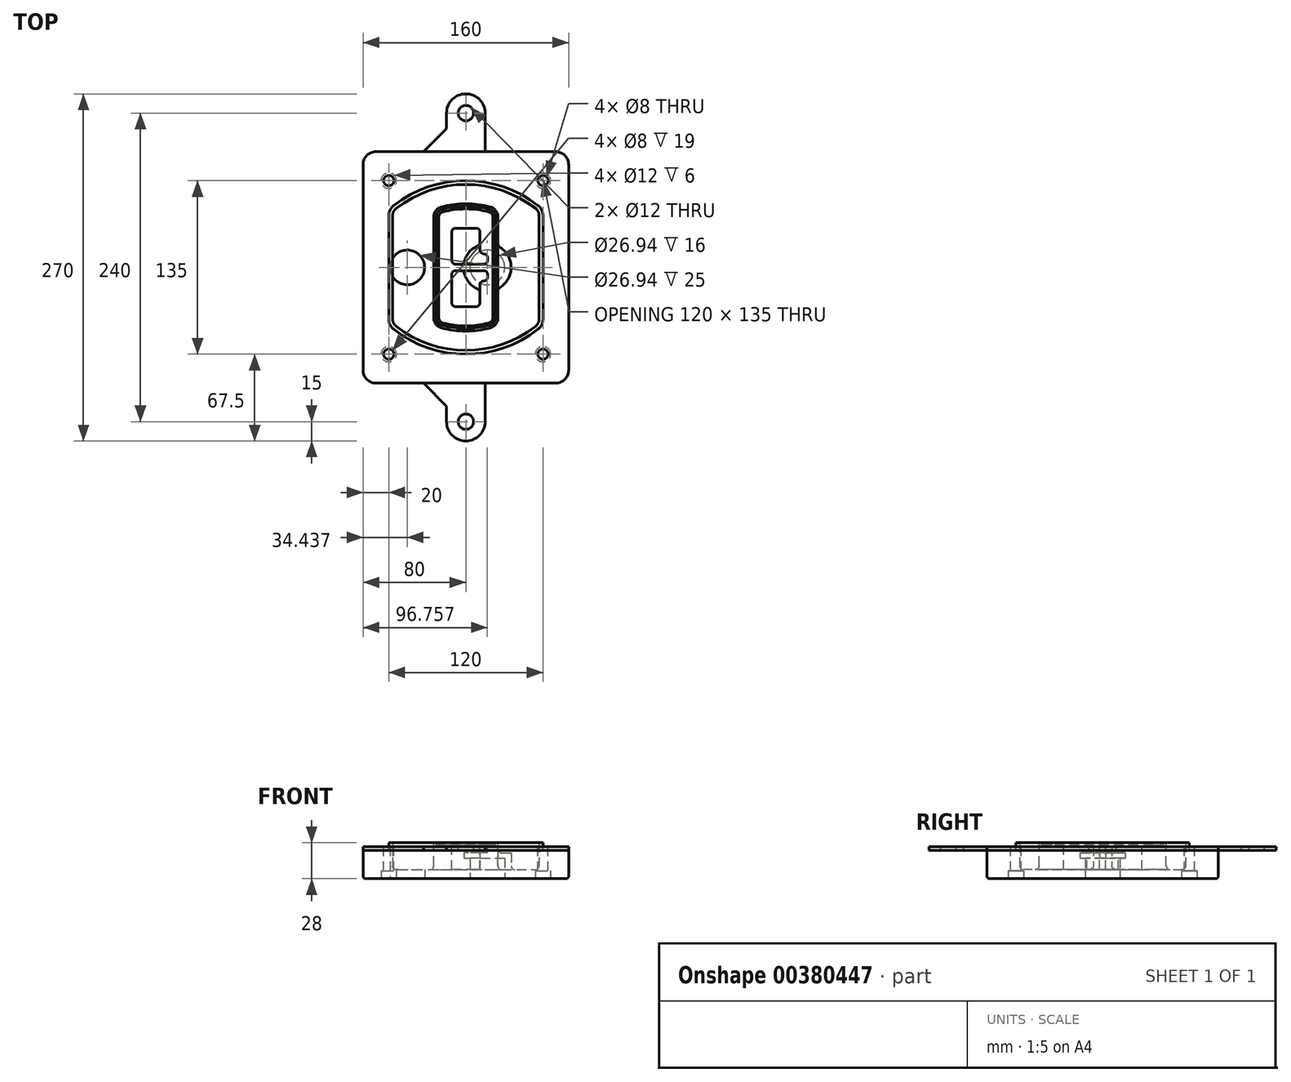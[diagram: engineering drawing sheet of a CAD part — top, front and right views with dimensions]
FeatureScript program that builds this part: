
annotation { "Feature Type Name" : "Feature", "Feature Type Description" : "" }
export const myFeature = defineFeature(function(context is Context, id is Id, definition is map)
    precondition{}
    {
        {
            var Q0;
            Q0=qCreatedBy(makeId("Top.planeOp"),FACE);
            var sketch = newSketch(context, id + "F0", { "sketchPlane" : qUnion([Q0])});
            skPoint(sketch, "E0.rect.middle", {"position": v(0, 0) * mm});
            skLineSegment(sketch, "E1.bottom", {"start": v(-70, -90) * mm, "end": v(70, -90) * mm});
            skLineSegment(sketch, "E1.top", {"start": v(-70, 90) * mm, "end": v(70, 90) * mm});
            skLineSegment(sketch, "E1.left", {"start": v(-80, -80) * mm, "end": v(-80, 80) * mm});
            skLineSegment(sketch, "E1.right", {"start": v(80, -80) * mm, "end": v(80, 80) * mm});
            skLineSegment(sketch, "E2", {"start": v(-80, 90) * mm, "end": v(80, -90) * mm, "construction": true});
            skLineSegment(sketch, "E3", {"start": v(80, 90) * mm, "end": v(-80, -90) * mm, "construction": true});
            skCircle(sketch, "E4", {"center": v(-60, 67.5) * mm, "radius": 4 * mm});
            skCircle(sketch, "E5", {"center": v(60, 67.5) * mm, "radius": 4 * mm});
            skCircle(sketch, "E6", {"center": v(60, -67.5) * mm, "radius": 4 * mm});
            skCircle(sketch, "E7", {"center": v(-60, -67.5) * mm, "radius": 4 * mm});
            skLineSegment(sketch, "E8", {"start": v(-60, 67.5) * mm, "end": v(60, 67.5) * mm, "construction": true});
            skLineSegment(sketch, "E9", {"start": v(60, 67.5) * mm, "end": v(60, -67.5) * mm, "construction": true});
            skLineSegment(sketch, "E10", {"start": v(60, -67.5) * mm, "end": v(-60, -67.5) * mm, "construction": true});
            skLineSegment(sketch, "E11", {"start": v(-60, -67.5) * mm, "end": v(-60, 67.5) * mm, "construction": true});
            skLineSegment(sketch, "E12", {"start": v(-60, 40.3) * mm, "end": v(-60, -40.3) * mm});
            skLineSegment(sketch, "E13", {"start": v(60, 40.3) * mm, "end": v(60, -40.3) * mm});
            skArc(sketch, "E14", {"start": v(56.15, 48.18) * mm, "mid": v(0, 67.5) * mm, "end": v(-56.15, 48.18) * mm});
            skArc(sketch, "E15", {"start": v(-56.15, -48.18) * mm, "mid": v(0, -67.5) * mm, "end": v(56.15, -48.18) * mm});
            skLineSegment(sketch, "E16", {"start": v(-60, 0) * mm, "end": v(60, 0) * mm, "construction": true});
            skPoint(sketch, "E17.visualSharp", {"position": v(-60, -45) * mm});
            skArc(sketch, "E17.filletArc", {"start": v(-60, -40.3) * mm, "mid": v(-58.99, -44.68) * mm, "end": v(-56.15, -48.18) * mm});
            skPoint(sketch, "E18.visualSharp", {"position": v(-60, 45) * mm});
            skArc(sketch, "E18.filletArc", {"start": v(-56.15, 48.18) * mm, "mid": v(-58.99, 44.68) * mm, "end": v(-60, 40.3) * mm});
            skPoint(sketch, "E19.visualSharp", {"position": v(60, 45) * mm});
            skArc(sketch, "E19.filletArc", {"start": v(60, 40.3) * mm, "mid": v(58.99, 44.68) * mm, "end": v(56.15, 48.18) * mm});
            skPoint(sketch, "E20.visualSharp", {"position": v(60, -45) * mm});
            skArc(sketch, "E20.filletArc", {"start": v(56.15, -48.18) * mm, "mid": v(58.99, -44.68) * mm, "end": v(60, -40.3) * mm});
            skPoint(sketch, "E21.visualSharp", {"position": v(-80, 90) * mm});
            skArc(sketch, "E21.filletArc", {"start": v(-70, 90) * mm, "mid": v(-77.07, 87.07) * mm, "end": v(-80, 80) * mm});
            skPoint(sketch, "E22.visualSharp", {"position": v(80, 90) * mm});
            skArc(sketch, "E22.filletArc", {"start": v(80, 80) * mm, "mid": v(77.07, 87.07) * mm, "end": v(70, 90) * mm});
            skPoint(sketch, "E23.visualSharp", {"position": v(80, -90) * mm});
            skArc(sketch, "E23.filletArc", {"start": v(70, -90) * mm, "mid": v(77.07, -87.07) * mm, "end": v(80, -80) * mm});
            skPoint(sketch, "E24.visualSharp", {"position": v(-80, -90) * mm});
            skArc(sketch, "E24.filletArc", {"start": v(-80, -80) * mm, "mid": v(-77.07, -87.07) * mm, "end": v(-70, -90) * mm});
            skArc(sketch, "E25.0", {"start": v(57, 40.3) * mm, "mid": v(56.3, 43.36) * mm, "end": v(54.3, 45.81) * mm});
            skLineSegment(sketch, "E25.1", {"start": v(57, 40.3) * mm, "end": v(57, -40.3) * mm});
            skArc(sketch, "E25.2", {"start": v(54.3, -45.81) * mm, "mid": v(56.3, -43.36) * mm, "end": v(57, -40.3) * mm});
            skArc(sketch, "E25.3", {"start": v(-54.3, -45.81) * mm, "mid": v(0, -64.5) * mm, "end": v(54.3, -45.81) * mm});
            skArc(sketch, "E25.4", {"start": v(-57, -40.3) * mm, "mid": v(-56.3, -43.36) * mm, "end": v(-54.3, -45.81) * mm});
            skArc(sketch, "E25.5", {"start": v(54.3, 45.81) * mm, "mid": v(0, 64.5) * mm, "end": v(-54.3, 45.81) * mm});
            skLineSegment(sketch, "E25.6", {"start": v(-57, 40.3) * mm, "end": v(-57, -40.3) * mm});
            skArc(sketch, "E25.7", {"start": v(-54.3, 45.81) * mm, "mid": v(-56.3, 43.36) * mm, "end": v(-57, 40.3) * mm});
            skArc(sketch, "E26.0", {"start": v(-58.62, 51.33) * mm, "mid": v(-62.58, 46.43) * mm, "end": v(-64, 40.3) * mm});
            skArc(sketch, "E26.1", {"start": v(58.62, 51.33) * mm, "mid": v(0, 71.5) * mm, "end": v(-58.62, 51.33) * mm});
            skArc(sketch, "E26.2", {"start": v(64, 40.3) * mm, "mid": v(62.58, 46.43) * mm, "end": v(58.62, 51.33) * mm});
            skLineSegment(sketch, "E26.3", {"start": v(64, 40.3) * mm, "end": v(64, -40.3) * mm});
            skArc(sketch, "E26.4", {"start": v(58.62, -51.33) * mm, "mid": v(62.58, -46.43) * mm, "end": v(64, -40.3) * mm});
            skLineSegment(sketch, "E26.5", {"start": v(-64, 40.3) * mm, "end": v(-64, -40.3) * mm});
            skArc(sketch, "E26.6", {"start": v(-58.62, -51.33) * mm, "mid": v(0, -71.5) * mm, "end": v(58.62, -51.33) * mm});
            skArc(sketch, "E26.7", {"start": v(-64, -40.3) * mm, "mid": v(-62.58, -46.43) * mm, "end": v(-58.62, -51.33) * mm});
            skSolve(sketch);
        }
        {
            var Q0;
            Q0=makeQuery(id+"F0.imprint","IMPRINT",FACE,{"disambiguationData":[TD([[makeQuery(id+"F0.imprint","IMPRINT",EDGE,{"derivedFrom":sQuery(id+"F0.wireOp",EDGE,"E1.bottom")}),1.0]])]});
            var Q1;
            Q1=makeQuery(id+"F0.imprint","IMPRINT",FACE,{"disambiguationData":[TD([[makeQuery(id+"F0.imprint","IMPRINT",EDGE,{"derivedFrom":sQuery(id+"F0.wireOp",EDGE,"E12")}),1.0]])]});
            var Q2;
            Q2=makeQuery(id+"F0.imprint","IMPRINT",FACE,{"disambiguationData":[TD([[makeQuery(id+"F0.imprint","IMPRINT",EDGE,{"derivedFrom":sQuery(id+"F0.wireOp",EDGE,"E25.0")}),1.0]])]});
            var Q3;
            Q3=makeQuery(id+"F0.imprint","IMPRINT",FACE,{"disambiguationData":[TD([[makeQuery(id+"F0.imprint","IMPRINT",EDGE,{"derivedFrom":sQuery(id+"F0.wireOp",EDGE,"E12")}),-1.0]])]});
            extrude(context, id + "F1", {"entities" : qUnion([Q0, Q1, Q2, Q3]), "oppositeDirection" : true, "depth" : 25 * mm});
        }
        {
            var Q0;
            Q0=makeQuery(id+"F0.imprint","IMPRINT",FACE,{"disambiguationData":[TD([[makeQuery(id+"F0.imprint","IMPRINT",EDGE,{"derivedFrom":sQuery(id+"F0.wireOp",EDGE,"E12")}),1.0]])]});
            extrude(context, id + "F2", {"entities" : qUnion([Q0]), "operationType" : NewBodyOperationType.ADD, "depth" : 3 * mm});
        }
        {
            var Q0;
            Q0=makeQuery(id+"F0.imprint","IMPRINT",FACE,{"disambiguationData":[TD([[makeQuery(id+"F0.imprint","IMPRINT",EDGE,{"derivedFrom":sQuery(id+"F0.wireOp",EDGE,"E25.0")}),1.0]])]});
            extrude(context, id + "F3", {"entities" : qUnion([Q0]), "operationType" : NewBodyOperationType.REMOVE, "oppositeDirection" : true, "depth" : 18 * mm});
        }
        {
            var Q0;
            Q0=makeQuery(id+"F2.opExtrude","CAP_FACE",FACE,{"disambiguationData":[OSD([sQuery(id+"F0.wireOp",EDGE,"E12"),sQuery(id+"F0.wireOp",EDGE,"E13"),sQuery(id+"F0.wireOp",EDGE,"E14"),sQuery(id+"F0.wireOp",EDGE,"E15"),sQuery(id+"F0.wireOp",EDGE,"E17.filletArc"),sQuery(id+"F0.wireOp",EDGE,"E18.filletArc"),sQuery(id+"F0.wireOp",EDGE,"E19.filletArc"),sQuery(id+"F0.wireOp",EDGE,"E20.filletArc"),sQuery(id+"F0.wireOp",EDGE,"E25.0"),sQuery(id+"F0.wireOp",EDGE,"E25.1"),sQuery(id+"F0.wireOp",EDGE,"E25.2"),sQuery(id+"F0.wireOp",EDGE,"E25.3"),sQuery(id+"F0.wireOp",EDGE,"E25.4"),sQuery(id+"F0.wireOp",EDGE,"E25.5"),sQuery(id+"F0.wireOp",EDGE,"E25.6"),sQuery(id+"F0.wireOp",EDGE,"E25.7")])],"isStart":false});
            var sketch = newSketch(context, id + "F4", { "sketchPlane" : qUnion([Q0])});
            skArc(sketch, "E27.0", {"start": v(-19.08, -46.97) * mm, "mid": v(0, -49.5) * mm, "end": v(19.08, -46.97) * mm});
            skArc(sketch, "E28.0", {"start": v(19.08, 46.97) * mm, "mid": v(0, 49.5) * mm, "end": v(-19.08, 46.97) * mm});
            skLineSegment(sketch, "E29", {"start": v(-25, 39.25) * mm, "end": v(-25, -39.25) * mm});
            skLineSegment(sketch, "E30", {"start": v(25, 39.25) * mm, "end": v(25, -39.25) * mm});
            skLineSegment(sketch, "E31", {"start": v(-25, 45.1) * mm, "end": v(25, 45.1) * mm, "construction": true});
            skLineSegment(sketch, "E32", {"start": v(-25, -45.1) * mm, "end": v(25, -45.1) * mm, "construction": true});
            skPoint(sketch, "E33.visualSharp", {"position": v(-25, 45.1) * mm});
            skArc(sketch, "E33.filletArc", {"start": v(-19.08, 46.97) * mm, "mid": v(-23.35, 44.11) * mm, "end": v(-25, 39.25) * mm});
            skPoint(sketch, "E34.visualSharp", {"position": v(25, 45.1) * mm});
            skArc(sketch, "E34.filletArc", {"start": v(25, 39.25) * mm, "mid": v(23.35, 44.11) * mm, "end": v(19.08, 46.97) * mm});
            skPoint(sketch, "E35.visualSharp", {"position": v(25, -45.1) * mm});
            skArc(sketch, "E35.filletArc", {"start": v(19.08, -46.97) * mm, "mid": v(23.35, -44.11) * mm, "end": v(25, -39.25) * mm});
            skPoint(sketch, "E36.visualSharp", {"position": v(-25, -45.1) * mm});
            skArc(sketch, "E36.filletArc", {"start": v(-25, -39.25) * mm, "mid": v(-23.35, -44.11) * mm, "end": v(-19.08, -46.97) * mm});
            skArc(sketch, "E37.0", {"start": v(54.3, 45.81) * mm, "mid": v(0, 64.5) * mm, "end": v(-54.3, 45.81) * mm});
            skArc(sketch, "E37.1", {"start": v(-54.3, 45.81) * mm, "mid": v(-56.3, 43.36) * mm, "end": v(-57, 40.3) * mm});
            skLineSegment(sketch, "E37.2", {"start": v(-57, 40.3) * mm, "end": v(-57, -40.3) * mm});
            skArc(sketch, "E37.3", {"start": v(-57, -40.3) * mm, "mid": v(-56.3, -43.36) * mm, "end": v(-54.3, -45.81) * mm});
            skArc(sketch, "E37.4", {"start": v(-54.3, -45.81) * mm, "mid": v(0, -64.5) * mm, "end": v(54.3, -45.81) * mm});
            skArc(sketch, "E37.5", {"start": v(54.3, -45.81) * mm, "mid": v(56.3, -43.36) * mm, "end": v(57, -40.3) * mm});
            skLineSegment(sketch, "E37.6", {"start": v(57, 40.3) * mm, "end": v(57, -40.3) * mm});
            skArc(sketch, "E37.7", {"start": v(57, 40.3) * mm, "mid": v(56.3, 43.36) * mm, "end": v(54.3, 45.81) * mm});
            skLineSegment(sketch, "E38.0", {"start": v(23, 39.25) * mm, "end": v(23, -39.25) * mm});
            skArc(sketch, "E38.1", {"start": v(18.56, -45.04) * mm, "mid": v(21.76, -42.9) * mm, "end": v(23, -39.25) * mm});
            skArc(sketch, "E38.2", {"start": v(-18.56, -45.04) * mm, "mid": v(0, -47.5) * mm, "end": v(18.56, -45.04) * mm});
            skArc(sketch, "E38.3", {"start": v(-23, -39.25) * mm, "mid": v(-21.76, -42.9) * mm, "end": v(-18.56, -45.04) * mm});
            skLineSegment(sketch, "E38.4", {"start": v(-23, 39.25) * mm, "end": v(-23, -39.25) * mm});
            skArc(sketch, "E38.5", {"start": v(23, 39.25) * mm, "mid": v(21.76, 42.9) * mm, "end": v(18.56, 45.04) * mm});
            skArc(sketch, "E38.6", {"start": v(-18.56, 45.04) * mm, "mid": v(-21.76, 42.9) * mm, "end": v(-23, 39.25) * mm});
            skArc(sketch, "E38.7", {"start": v(18.56, 45.04) * mm, "mid": v(0, 47.5) * mm, "end": v(-18.56, 45.04) * mm});
            skArc(sketch, "E39.0", {"start": v(21, 39.25) * mm, "mid": v(20.18, 41.68) * mm, "end": v(18.04, 43.1) * mm});
            skLineSegment(sketch, "E39.1", {"start": v(21, 39.25) * mm, "end": v(21, -39.25) * mm});
            skArc(sketch, "E39.2", {"start": v(18.04, -43.1) * mm, "mid": v(20.18, -41.68) * mm, "end": v(21, -39.25) * mm});
            skArc(sketch, "E39.3", {"start": v(-18.04, -43.1) * mm, "mid": v(0, -45.5) * mm, "end": v(18.04, -43.1) * mm});
            skArc(sketch, "E39.4", {"start": v(-21, -39.25) * mm, "mid": v(-20.18, -41.68) * mm, "end": v(-18.04, -43.1) * mm});
            skArc(sketch, "E39.5", {"start": v(18.04, 43.1) * mm, "mid": v(0, 45.5) * mm, "end": v(-18.04, 43.1) * mm});
            skLineSegment(sketch, "E39.6", {"start": v(-21, 39.25) * mm, "end": v(-21, -39.25) * mm});
            skArc(sketch, "E39.7", {"start": v(-18.04, 43.1) * mm, "mid": v(-20.18, 41.68) * mm, "end": v(-21, 39.25) * mm});
            skLineSegment(sketch, "E40", {"start": v(-25, 0) * mm, "end": v(25, 0) * mm, "construction": true});
            skLineSegment(sketch, "E41", {"start": v(-11, 5.5) * mm, "end": v(-11, 27.5) * mm});
            skLineSegment(sketch, "E42", {"start": v(-8, 30.5) * mm, "end": v(8, 30.5) * mm});
            skLineSegment(sketch, "E43", {"start": v(11, 27.5) * mm, "end": v(11, 13.5) * mm});
            skLineSegment(sketch, "E44", {"start": v(14, 10.5) * mm, "end": v(14, 10.5) * mm});
            skLineSegment(sketch, "E45", {"start": v(17, 7.5) * mm, "end": v(17, 5.5) * mm});
            skLineSegment(sketch, "E46", {"start": v(14, 2.5) * mm, "end": v(-8, 2.5) * mm});
            skPoint(sketch, "E47.visualSharp", {"position": v(-11, 30.5) * mm});
            skArc(sketch, "E47.filletArc", {"start": v(-8, 30.5) * mm, "mid": v(-10.12, 29.62) * mm, "end": v(-11, 27.5) * mm});
            skPoint(sketch, "E48.visualSharp", {"position": v(11, 30.5) * mm});
            skArc(sketch, "E48.filletArc", {"start": v(11, 27.5) * mm, "mid": v(10.12, 29.62) * mm, "end": v(8, 30.5) * mm});
            skPoint(sketch, "E49.visualSharp", {"position": v(11, 10.5) * mm});
            skArc(sketch, "E49.filletArc", {"start": v(11, 13.5) * mm, "mid": v(11.88, 11.38) * mm, "end": v(14, 10.5) * mm});
            skPoint(sketch, "E50.visualSharp", {"position": v(17, 10.5) * mm});
            skArc(sketch, "E50.filletArc", {"start": v(17, 7.5) * mm, "mid": v(16.12, 9.62) * mm, "end": v(14, 10.5) * mm});
            skPoint(sketch, "E51.visualSharp", {"position": v(17, 2.5) * mm});
            skArc(sketch, "E51.filletArc", {"start": v(14, 2.5) * mm, "mid": v(16.12, 3.38) * mm, "end": v(17, 5.5) * mm});
            skPoint(sketch, "E52.visualSharp", {"position": v(-11, 2.5) * mm});
            skArc(sketch, "E52.filletArc", {"start": v(-11, 5.5) * mm, "mid": v(-10.12, 3.38) * mm, "end": v(-8, 2.5) * mm});
            skLineSegment(sketch, "E53.0.MirrorCS", {"start": v(14, -2.5) * mm, "end": v(-8, -2.5) * mm});
            skArc(sketch, "E54.0.MirrorCS", {"start": v(-11, -5.5) * mm, "mid": v(-10.12, -3.38) * mm, "end": v(-8, -2.5) * mm});
            skLineSegment(sketch, "E55.0.MirrorCS", {"start": v(-11, -5.5) * mm, "end": v(-11, -27.5) * mm});
            skArc(sketch, "E56.0.MirrorCS", {"start": v(-8, -30.5) * mm, "mid": v(-10.12, -29.62) * mm, "end": v(-11, -27.5) * mm});
            skLineSegment(sketch, "E57.0.MirrorCS", {"start": v(-8, -30.5) * mm, "end": v(8, -30.5) * mm});
            skArc(sketch, "E58.0.MirrorCS", {"start": v(11, -27.5) * mm, "mid": v(10.12, -29.62) * mm, "end": v(8, -30.5) * mm});
            skLineSegment(sketch, "E59.0.MirrorCS", {"start": v(11, -27.5) * mm, "end": v(11, -13.5) * mm});
            skArc(sketch, "E60.0.MirrorCS", {"start": v(11, -13.5) * mm, "mid": v(11.88, -11.38) * mm, "end": v(14, -10.5) * mm});
            skArc(sketch, "E61.0.MirrorCS", {"start": v(17, -7.5) * mm, "mid": v(16.12, -9.62) * mm, "end": v(14, -10.5) * mm});
            skLineSegment(sketch, "E62.0.MirrorCS", {"start": v(17, -7.5) * mm, "end": v(17, -5.5) * mm});
            skArc(sketch, "E63.0.MirrorCS", {"start": v(14, -2.5) * mm, "mid": v(16.12, -3.38) * mm, "end": v(17, -5.5) * mm});
            skSolve(sketch);
        }
        {
            var Q0;
            Q0=makeQuery(id+"F4.imprint","IMPRINT",FACE,{"disambiguationData":[TD([[makeQuery(id+"F4.imprint","IMPRINT",EDGE,{"derivedFrom":sQuery(id+"F4.wireOp",EDGE,"E27.0")}),1.0]])]});
            var Q1;
            Q1=makeQuery(id+"F4.imprint","IMPRINT",FACE,{"disambiguationData":[TD([[makeQuery(id+"F4.imprint","IMPRINT",EDGE,{"derivedFrom":sQuery(id+"F4.wireOp",EDGE,"E38.0")}),-1.0]])]});
            var Q2;
            Q2=makeQuery(id+"F4.imprint","IMPRINT",FACE,{"disambiguationData":[TD([[makeQuery(id+"F4.imprint","IMPRINT",EDGE,{"derivedFrom":sQuery(id+"F4.wireOp",EDGE,"E39.0")}),1.0]])]});
            extrude(context, id + "F5", {"entities" : qUnion([Q0, Q1, Q2]), "operationType" : NewBodyOperationType.ADD, "endBound" : BoundingType.UP_TO_NEXT, "oppositeDirection" : true, "depth" : 25 * mm});
        }
        {
            var Q0;
            Q0=makeQuery(id+"F4.imprint","IMPRINT",FACE,{"disambiguationData":[TD([[makeQuery(id+"F4.imprint","IMPRINT",EDGE,{"derivedFrom":sQuery(id+"F4.wireOp",EDGE,"E38.0")}),-1.0]])]});
            extrude(context, id + "F6", {"entities" : qUnion([Q0]), "operationType" : NewBodyOperationType.REMOVE, "oppositeDirection" : true, "depth" : 2 * mm});
        }
        {
            var Q0;
            Q0=makeQuery(id+"F1.opExtrude","CAP_FACE",FACE,{"disambiguationData":[OSD([sQuery(id+"F0.wireOp",EDGE,"E1.bottom"),sQuery(id+"F0.wireOp",EDGE,"E1.top"),sQuery(id+"F0.wireOp",EDGE,"E1.left"),sQuery(id+"F0.wireOp",EDGE,"E1.right"),sQuery(id+"F0.wireOp",EDGE,"E4"),sQuery(id+"F0.wireOp",EDGE,"E5"),sQuery(id+"F0.wireOp",EDGE,"E6"),sQuery(id+"F0.wireOp",EDGE,"E7"),sQuery(id+"F0.wireOp",EDGE,"E21.filletArc"),sQuery(id+"F0.wireOp",EDGE,"E22.filletArc"),sQuery(id+"F0.wireOp",EDGE,"E23.filletArc"),sQuery(id+"F0.wireOp",EDGE,"E24.filletArc")])],"isStart":false});
            var sketch = newSketch(context, id + "F7", { "sketchPlane" : qUnion([Q0])});
            skCircle(sketch, "E64", {"center": v(16.76, 0) * mm, "radius": 13.47 * mm});
            skCircle(sketch, "E65", {"center": v(-45.56, 0) * mm, "radius": 13.47 * mm});
            skLineSegment(sketch, "E66", {"start": v(80, 0) * mm, "end": v(-80, 0) * mm});
            skCircle(sketch, "E67", {"center": v(16.76, 0) * mm, "radius": 18.47 * mm});
            skCircle(sketch, "E68", {"center": v(60, -67.5) * mm, "radius": 6 * mm});
            skCircle(sketch, "E69", {"center": v(-60, -67.5) * mm, "radius": 6 * mm});
            skCircle(sketch, "E70", {"center": v(-60, 67.5) * mm, "radius": 6 * mm});
            skCircle(sketch, "E71", {"center": v(60, 67.5) * mm, "radius": 6 * mm});
            skSolve(sketch);
        }
        {
            var Q0;
            {var subQ1=sQuery(id+"F7.wireOp",EDGE,"E66");var subQ4=sQuery(id+"F7.wireOp",EDGE,"E64");var subQ6=makeQuery(id+"F7.imprint","INTERSECT",VERTEX,{"disambiguationData":[OD(0.0)],"derivedFrom":[subQ4,subQ1]});Q0=makeQuery(id+"F7.imprint","IMPRINT",FACE,{"disambiguationData":[TD([[makeQuery(id+"F7.imprint","IMPRINT",EDGE,{"disambiguationData":[TD([[subQ6,-1.0]])],"derivedFrom":subQ4}),-1.0]])]});}
            var Q1;
            {var subQ0=sQuery(id+"F7.wireOp",EDGE,"E66");var subQ1=sQuery(id+"F7.wireOp",EDGE,"E64");var subQ3=makeQuery(id+"F7.imprint","INTERSECT",VERTEX,{"disambiguationData":[OD(0.0)],"derivedFrom":[subQ1,subQ0]});Q1=makeQuery(id+"F7.imprint","IMPRINT",FACE,{"disambiguationData":[TD([[makeQuery(id+"F7.imprint","IMPRINT",EDGE,{"disambiguationData":[TD([[subQ3,-1.0]])],"derivedFrom":subQ1}),1.0]])]});}
            var Q2;
            {var subQ0=sQuery(id+"F7.wireOp",EDGE,"E66");var subQ1=sQuery(id+"F7.wireOp",EDGE,"E64");var subQ3=makeQuery(id+"F7.imprint","INTERSECT",VERTEX,{"disambiguationData":[OD(0.0)],"derivedFrom":[subQ1,subQ0]});Q2=makeQuery(id+"F7.imprint","IMPRINT",FACE,{"disambiguationData":[TD([[makeQuery(id+"F7.imprint","IMPRINT",EDGE,{"disambiguationData":[TD([[subQ3,1.0]])],"derivedFrom":subQ1}),1.0]])]});}
            var Q3;
            {var subQ1=sQuery(id+"F7.wireOp",EDGE,"E66");var subQ4=sQuery(id+"F7.wireOp",EDGE,"E64");var subQ6=makeQuery(id+"F7.imprint","INTERSECT",VERTEX,{"disambiguationData":[OD(0.0)],"derivedFrom":[subQ4,subQ1]});Q3=makeQuery(id+"F7.imprint","IMPRINT",FACE,{"disambiguationData":[TD([[makeQuery(id+"F7.imprint","IMPRINT",EDGE,{"disambiguationData":[TD([[subQ6,1.0]])],"derivedFrom":subQ4}),-1.0]])]});}
            extrude(context, id + "F8", {"entities" : qUnion([Q0, Q1, Q2, Q3]), "operationType" : NewBodyOperationType.ADD, "oppositeDirection" : true, "depth" : 20 * mm});
        }
        {
            var Q0;
            {var subQ0=sQuery(id+"F7.wireOp",EDGE,"E66");var subQ1=sQuery(id+"F7.wireOp",EDGE,"E64");var subQ3=makeQuery(id+"F7.imprint","INTERSECT",VERTEX,{"disambiguationData":[OD(0.0)],"derivedFrom":[subQ1,subQ0]});Q0=makeQuery(id+"F7.imprint","IMPRINT",FACE,{"disambiguationData":[TD([[makeQuery(id+"F7.imprint","IMPRINT",EDGE,{"disambiguationData":[TD([[subQ3,-1.0]])],"derivedFrom":subQ1}),1.0]])]});}
            var Q1;
            {var subQ0=sQuery(id+"F7.wireOp",EDGE,"E66");var subQ1=sQuery(id+"F7.wireOp",EDGE,"E64");var subQ3=makeQuery(id+"F7.imprint","INTERSECT",VERTEX,{"disambiguationData":[OD(0.0)],"derivedFrom":[subQ1,subQ0]});Q1=makeQuery(id+"F7.imprint","IMPRINT",FACE,{"disambiguationData":[TD([[makeQuery(id+"F7.imprint","IMPRINT",EDGE,{"disambiguationData":[TD([[subQ3,1.0]])],"derivedFrom":subQ1}),1.0]])]});}
            extrude(context, id + "F9", {"entities" : qUnion([Q0, Q1]), "operationType" : NewBodyOperationType.REMOVE, "oppositeDirection" : true, "depth" : 16 * mm});
        }
        {
            var Q0;
            {var subQ0=sQuery(id+"F7.wireOp",EDGE,"E66");var subQ1=sQuery(id+"F7.wireOp",EDGE,"E65");var subQ3=makeQuery(id+"F7.imprint","INTERSECT",VERTEX,{"disambiguationData":[OD(0.0)],"derivedFrom":[subQ1,subQ0]});Q0=makeQuery(id+"F7.imprint","IMPRINT",FACE,{"disambiguationData":[TD([[makeQuery(id+"F7.imprint","IMPRINT",EDGE,{"disambiguationData":[TD([[subQ3,-1.0]])],"derivedFrom":subQ1}),1.0]])]});}
            var Q1;
            {var subQ0=sQuery(id+"F7.wireOp",EDGE,"E66");var subQ1=sQuery(id+"F7.wireOp",EDGE,"E65");var subQ3=makeQuery(id+"F7.imprint","INTERSECT",VERTEX,{"disambiguationData":[OD(0.0)],"derivedFrom":[subQ1,subQ0]});Q1=makeQuery(id+"F7.imprint","IMPRINT",FACE,{"disambiguationData":[TD([[makeQuery(id+"F7.imprint","IMPRINT",EDGE,{"disambiguationData":[TD([[subQ3,1.0]])],"derivedFrom":subQ1}),1.0]])]});}
            extrude(context, id + "F10", {"entities" : qUnion([Q0, Q1]), "operationType" : NewBodyOperationType.REMOVE, "oppositeDirection" : true, "depth" : 25 * mm});
        }
        {
            var Q0;
            Q0=makeQuery(id+"F7.imprint","IMPRINT",FACE,{"disambiguationData":[TD([[makeQuery(id+"F7.imprint","IMPRINT",EDGE,{"derivedFrom":sQuery(id+"F7.wireOp",EDGE,"E68")}),1.0]])]});
            var Q1;
            Q1=makeQuery(id+"F7.imprint","IMPRINT",FACE,{"disambiguationData":[TD([[makeQuery(id+"F7.imprint","IMPRINT",EDGE,{"derivedFrom":makeQuery(id+"F1.opExtrude","CAP_EDGE",EDGE,{"disambiguationData":[OSD([sQuery(id+"F0.wireOp",EDGE,"E5")])],"isStart":false})}),-1.0]])]});
            var Q2;
            Q2=makeQuery(id+"F7.imprint","IMPRINT",FACE,{"disambiguationData":[TD([[makeQuery(id+"F7.imprint","IMPRINT",EDGE,{"derivedFrom":sQuery(id+"F7.wireOp",EDGE,"E69")}),1.0]])]});
            var Q3;
            Q3=makeQuery(id+"F7.imprint","IMPRINT",FACE,{"disambiguationData":[TD([[makeQuery(id+"F7.imprint","IMPRINT",EDGE,{"derivedFrom":makeQuery(id+"F1.opExtrude","CAP_EDGE",EDGE,{"disambiguationData":[OSD([sQuery(id+"F0.wireOp",EDGE,"E4")])],"isStart":false})}),-1.0]])]});
            var Q4;
            Q4=makeQuery(id+"F7.imprint","IMPRINT",FACE,{"disambiguationData":[TD([[makeQuery(id+"F7.imprint","IMPRINT",EDGE,{"derivedFrom":sQuery(id+"F7.wireOp",EDGE,"E70")}),1.0]])]});
            var Q5;
            Q5=makeQuery(id+"F7.imprint","IMPRINT",FACE,{"disambiguationData":[TD([[makeQuery(id+"F7.imprint","IMPRINT",EDGE,{"derivedFrom":makeQuery(id+"F1.opExtrude","CAP_EDGE",EDGE,{"disambiguationData":[OSD([sQuery(id+"F0.wireOp",EDGE,"E7")])],"isStart":false})}),-1.0]])]});
            var Q6;
            Q6=makeQuery(id+"F7.imprint","IMPRINT",FACE,{"disambiguationData":[TD([[makeQuery(id+"F7.imprint","IMPRINT",EDGE,{"derivedFrom":sQuery(id+"F7.wireOp",EDGE,"E71")}),1.0]])]});
            var Q7;
            Q7=makeQuery(id+"F7.imprint","IMPRINT",FACE,{"disambiguationData":[TD([[makeQuery(id+"F7.imprint","IMPRINT",EDGE,{"derivedFrom":makeQuery(id+"F1.opExtrude","CAP_EDGE",EDGE,{"disambiguationData":[OSD([sQuery(id+"F0.wireOp",EDGE,"E6")])],"isStart":false})}),-1.0]])]});
            extrude(context, id + "F11", {"entities" : qUnion([Q0, Q1, Q2, Q3, Q4, Q5, Q6, Q7]), "operationType" : NewBodyOperationType.REMOVE, "oppositeDirection" : true, "depth" : 6 * mm});
        }
        {
            var Q0;
            Q0=makeQuery(id+"F9.boolean.opBoolean","COPY",FACE,{"derivedFrom":makeQuery(id+"F9.opExtrude","CAP_FACE",FACE,{"disambiguationData":[OSD([sQuery(id+"F7.wireOp",EDGE,"E64")])],"isStart":false})});
            var sketch = newSketch(context, id + "F12", { "sketchPlane" : qUnion([Q0])});
            skArc(sketch, "E72.0", {"start": v(11, 17.55) * mm, "mid": v(2.57, 11.82) * mm, "end": v(-1.54, 2.5) * mm});
            skArc(sketch, "E72.1", {"start": v(-1.54, -2.5) * mm, "mid": v(2.57, -11.82) * mm, "end": v(11, -17.55) * mm});
            skLineSegment(sketch, "E73", {"start": v(-1.54, -2.5) * mm, "end": v(14, -2.5) * mm});
            skLineSegment(sketch, "E74.0", {"start": v(14, 2.5) * mm, "end": v(-1.54, 2.5) * mm});
            skArc(sketch, "E74.1", {"start": v(14, 2.5) * mm, "mid": v(16.12, 3.38) * mm, "end": v(17, 5.5) * mm});
            skLineSegment(sketch, "E74.2", {"start": v(17, 7.5) * mm, "end": v(17, 5.5) * mm});
            skArc(sketch, "E74.3", {"start": v(17, 7.5) * mm, "mid": v(16.12, 9.62) * mm, "end": v(14, 10.5) * mm});
            skArc(sketch, "E74.4", {"start": v(11, 13.5) * mm, "mid": v(11.88, 11.38) * mm, "end": v(14, 10.5) * mm});
            skLineSegment(sketch, "E74.5", {"start": v(11, 17.55) * mm, "end": v(11, 13.5) * mm});
            skLineSegment(sketch, "E74.7", {"start": v(14, -2.5) * mm, "end": v(-1.54, -2.5) * mm});
            skArc(sketch, "E74.8", {"start": v(14, -2.5) * mm, "mid": v(16.12, -3.38) * mm, "end": v(17, -5.5) * mm});
            skLineSegment(sketch, "E74.9", {"start": v(17, -7.5) * mm, "end": v(17, -5.5) * mm});
            skArc(sketch, "E74.10", {"start": v(17, -7.5) * mm, "mid": v(16.12, -9.62) * mm, "end": v(14, -10.5) * mm});
            skArc(sketch, "E74.11", {"start": v(11, -13.5) * mm, "mid": v(11.88, -11.38) * mm, "end": v(14, -10.5) * mm});
            skLineSegment(sketch, "E74.12", {"start": v(11, -17.55) * mm, "end": v(11, -13.5) * mm});
            skPoint(sketch, "E75.orphan", {"position": v(11, -27.5) * mm});
            skPoint(sketch, "E76.orphan", {"position": v(-8, -2.5) * mm});
            skPoint(sketch, "E77.orphan", {"position": v(-8, 2.5) * mm});
            skPoint(sketch, "E78.orphan", {"position": v(11, 27.5) * mm});
            skSolve(sketch);
        }
        {
            var Q0;
            {var subQ7=sQuery(id+"F12.wireOp",EDGE,"E72.0");var subQ14=sQuery(id+"F12.wireOp",EDGE,"E72.1");var subQ16=sQuery(id+"F12.wireOp",EDGE,"E74.1");var subQ18=sQuery(id+"F12.wireOp",EDGE,"E74.8");Q0=qUnion([makeQuery(id+"F12.imprint","IMPRINT",FACE,{"disambiguationData":[TD([[makeQuery(id+"F12.imprint","IMPRINT",EDGE,{"derivedFrom":subQ7}),1.0]])]}),makeQuery(id+"F12.imprint","IMPRINT",FACE,{"disambiguationData":[TD([[makeQuery(id+"F12.imprint","IMPRINT",EDGE,{"derivedFrom":subQ14}),1.0]])]}),makeQuery(id+"F12.imprint","IMPRINT",FACE,{"disambiguationData":[TD([[makeQuery(id+"F12.imprint","IMPRINT",EDGE,{"derivedFrom":subQ16}),1.0]])]}),makeQuery(id+"F12.imprint","IMPRINT",FACE,{"disambiguationData":[TD([[makeQuery(id+"F12.imprint","IMPRINT",EDGE,{"derivedFrom":subQ18}),-1.0]])]})]);}
            var Q1;
            Q1=makeQuery(id+"F5.boolean.opBoolean","SPLIT",FACE,{"disambiguationData":[TD([makeQuery(id+"F5.opExtrude","SWEPT_FACE",FACE,{"disambiguationData":[OSD([sQuery(id+"F4.wireOp",EDGE,"E41")])]})])],"derivedFrom":makeQuery(id+"F3.boolean.opBoolean","COPY",FACE,{"derivedFrom":makeQuery(id+"F3.opExtrude","CAP_FACE",FACE,{"disambiguationData":[OSD([sQuery(id+"F0.wireOp",EDGE,"E25.0"),sQuery(id+"F0.wireOp",EDGE,"E25.1"),sQuery(id+"F0.wireOp",EDGE,"E25.2"),sQuery(id+"F0.wireOp",EDGE,"E25.3"),sQuery(id+"F0.wireOp",EDGE,"E25.4"),sQuery(id+"F0.wireOp",EDGE,"E25.5"),sQuery(id+"F0.wireOp",EDGE,"E25.6"),sQuery(id+"F0.wireOp",EDGE,"E25.7")])],"isStart":false})})});
            extrude(context, id + "F13", {"entities" : qUnion([Q0]), "operationType" : NewBodyOperationType.REMOVE, "endBound" : BoundingType.UP_TO_SURFACE, "endBoundEntityFace" : qUnion([Q1]), "depth" : 25 * mm});
        }
        {
            var Q0;
            Q0=makeQuery(id+"F3.boolean.opBoolean","COPY",EDGE,{"derivedFrom":makeQuery(id+"F3.opExtrude","CAP_EDGE",EDGE,{"disambiguationData":[OSD([sQuery(id+"F0.wireOp",EDGE,"E25.6")])],"isStart":false})});
            var Q1;
            Q1=makeQuery(id+"F8.boolean.opBoolean","INTERSECT",EDGE,{"derivedFrom":[makeQuery(id+"F5.opExtrude","SWEPT_FACE",FACE,{"disambiguationData":[OSD([sQuery(id+"F4.wireOp",EDGE,"E30")])]}),makeQuery(id+"F8.opExtrude","CAP_FACE",FACE,{"disambiguationData":[OSD([sQuery(id+"F7.wireOp",EDGE,"E67")])],"isStart":false})]});
            var Q2;
            Q2=makeQuery(id+"F8.boolean.opBoolean","INTERSECT",EDGE,{"disambiguationData":[OD(1.0)],"derivedFrom":[makeQuery(id+"F5.opExtrude","SWEPT_FACE",FACE,{"disambiguationData":[OSD([sQuery(id+"F4.wireOp",EDGE,"E30")])]}),makeQuery(id+"F8.opExtrude","SWEPT_FACE",FACE,{"disambiguationData":[OSD([sQuery(id+"F7.wireOp",EDGE,"E67")])]})]});
            var Q3;
            {var subQ0=sQuery(id+"F4.wireOp",EDGE,"E30");Q3=makeQuery(id+"F8.boolean.opBoolean","SPLIT",EDGE,{"disambiguationData":[TD([makeQuery(id+"F5.opExtrude","SWEPT_FACE",FACE,{"disambiguationData":[OSD([sQuery(id+"F4.wireOp",EDGE,"E35.filletArc")])]})])],"derivedFrom":makeQuery(id+"F5.opExtrude","CAP_EDGE",EDGE,{"disambiguationData":[OSD([subQ0])],"isStart":false})});}
            var Q4;
            {var subQ0=sQuery(id+"F0.wireOp",EDGE,"E25.7");var subQ1=sQuery(id+"F0.wireOp",EDGE,"E25.1");var subQ2=sQuery(id+"F0.wireOp",EDGE,"E25.6");var subQ3=sQuery(id+"F0.wireOp",EDGE,"E25.5");var subQ4=sQuery(id+"F0.wireOp",EDGE,"E25.4");var subQ5=sQuery(id+"F0.wireOp",EDGE,"E25.0");var subQ6=sQuery(id+"F0.wireOp",EDGE,"E25.2");var subQ7=sQuery(id+"F0.wireOp",EDGE,"E25.3");Q4=makeQuery(id+"F8.boolean.opBoolean","INTERSECT",EDGE,{"derivedFrom":[makeQuery(id+"F5.boolean.opBoolean","SPLIT",FACE,{"disambiguationData":[TD([makeQuery(id+"F2.opExtrude","SWEPT_FACE",FACE,{"disambiguationData":[OSD([subQ5])]})])],"derivedFrom":makeQuery(id+"F3.boolean.opBoolean","COPY",FACE,{"derivedFrom":makeQuery(id+"F3.opExtrude","CAP_FACE",FACE,{"disambiguationData":[OSD([subQ5,subQ1,subQ6,subQ7,subQ4,subQ3,subQ2,subQ0])],"isStart":false})})}),makeQuery(id+"F8.opExtrude","SWEPT_FACE",FACE,{"disambiguationData":[OSD([sQuery(id+"F7.wireOp",EDGE,"E67")])]})]});}
            var Q5;
            Q5=makeQuery(id+"F8.boolean.opBoolean","INTERSECT",EDGE,{"disambiguationData":[OD(0.0)],"derivedFrom":[makeQuery(id+"F5.opExtrude","SWEPT_FACE",FACE,{"disambiguationData":[OSD([sQuery(id+"F4.wireOp",EDGE,"E30")])]}),makeQuery(id+"F8.opExtrude","SWEPT_FACE",FACE,{"disambiguationData":[OSD([sQuery(id+"F7.wireOp",EDGE,"E67")])]})]});
            fillet(context, id + "F14", {"entities" : qUnion([Q0, Q1, Q2, Q3, Q4, Q5]), "radius" : 3 * mm, "tangentPropagation" : true, "allowEdgeOverflow" : false});
        }
        {
            var Q0;
            Q0=makeQuery(id+"F1.opExtrude","CAP_EDGE",EDGE,{"disambiguationData":[OSD([sQuery(id+"F0.wireOp",EDGE,"E1.bottom")])],"isStart":false});
            fillet(context, id + "F15", {"entities" : qUnion([Q0]), "radius" : 2 * mm, "tangentPropagation" : true, "allowEdgeOverflow" : false});
        }
        {
            var Q0;
            {var subQ0=sQuery(id+"F0.wireOp",EDGE,"E21.filletArc");var subQ1=sQuery(id+"F0.wireOp",EDGE,"E7");var subQ2=sQuery(id+"F0.wireOp",EDGE,"E6");var subQ3=sQuery(id+"F0.wireOp",EDGE,"E5");var subQ4=sQuery(id+"F0.wireOp",EDGE,"E4");var subQ5=sQuery(id+"F0.wireOp",EDGE,"E22.filletArc");var subQ6=sQuery(id+"F0.wireOp",EDGE,"E1.bottom");var subQ7=sQuery(id+"F0.wireOp",EDGE,"E1.right");var subQ8=sQuery(id+"F0.wireOp",EDGE,"E1.top");var subQ9=sQuery(id+"F0.wireOp",EDGE,"E1.left");var subQ10=sQuery(id+"F0.wireOp",EDGE,"E23.filletArc");var subQ11=sQuery(id+"F0.wireOp",EDGE,"E24.filletArc");Q0=makeQuery(id+"F2.boolean.opBoolean","SPLIT",FACE,{"disambiguationData":[TD([makeQuery(id+"F1.opExtrude","SWEPT_FACE",FACE,{"disambiguationData":[OSD([subQ6])]})])],"derivedFrom":makeQuery(id+"F1.opExtrude","CAP_FACE",FACE,{"disambiguationData":[OSD([subQ6,subQ8,subQ9,subQ7,subQ4,subQ3,subQ2,subQ1,subQ0,subQ5,subQ10,subQ11])],"isStart":true})});}
            var sketch = newSketch(context, id + "F16", { "sketchPlane" : qUnion([Q0])});
            skLineSegment(sketch, "E79", {"start": v(-33, 90) * mm, "end": v(-15, 108) * mm});
            skLineSegment(sketch, "E80", {"start": v(15, 90) * mm, "end": v(15, 90) * mm});
            skLineSegment(sketch, "E81", {"start": v(-15, 108) * mm, "end": v(-15, 120) * mm});
            skLineSegment(sketch, "E82", {"start": v(15, 90) * mm, "end": v(15, 120) * mm});
            skArc(sketch, "E83", {"start": v(15, 120) * mm, "mid": v(0, 135) * mm, "end": v(-15, 120) * mm});
            skCircle(sketch, "E84", {"center": v(0, 120) * mm, "radius": 6 * mm});
            skLineSegment(sketch, "E85", {"start": v(-80, 0) * mm, "end": v(80, 0) * mm, "construction": true});
            skArc(sketch, "E86.MirrorCS", {"start": v(15, -120) * mm, "mid": v(0, -135) * mm, "end": v(-15, -120) * mm});
            skLineSegment(sketch, "E87.MirrorCS", {"start": v(-15, -108) * mm, "end": v(-15, -120) * mm});
            skLineSegment(sketch, "E88.MirrorCS", {"start": v(-33, -90) * mm, "end": v(-15, -108) * mm});
            skCircle(sketch, "E89.MirrorC", {"center": v(0, -120) * mm, "radius": 6 * mm});
            skLineSegment(sketch, "E90.MirrorCS", {"start": v(15, -90) * mm, "end": v(15, -120) * mm});
            skLineSegment(sketch, "E91.MirrorCS", {"start": v(15, -90) * mm, "end": v(15, -90) * mm});
            skLineSegment(sketch, "E92", {"start": v(-33, 90) * mm, "end": v(15, 90) * mm});
            skLineSegment(sketch, "E93", {"start": v(-33, -90) * mm, "end": v(15, -90) * mm});
            skSolve(sketch);
        }
        {
            var Q0;
            Q0 = qSketchRegion(id + "F16", true);
            var Q1;
            {var subQ4=sQuery(id+"F16.wireOp",EDGE,"E92");Q1=makeQuery(id+"F16.imprint","IMPRINT",FACE,{"disambiguationData":[TD([[makeQuery(id+"F16.imprint","IMPRINT",EDGE,{"derivedFrom":subQ4}),-1.0]])]});}
            extrude(context, id + "F17", {"entities" : qUnion([Q0, Q1]), "oppositeDirection" : true, "depth" : 3 * mm});
        }
    });
